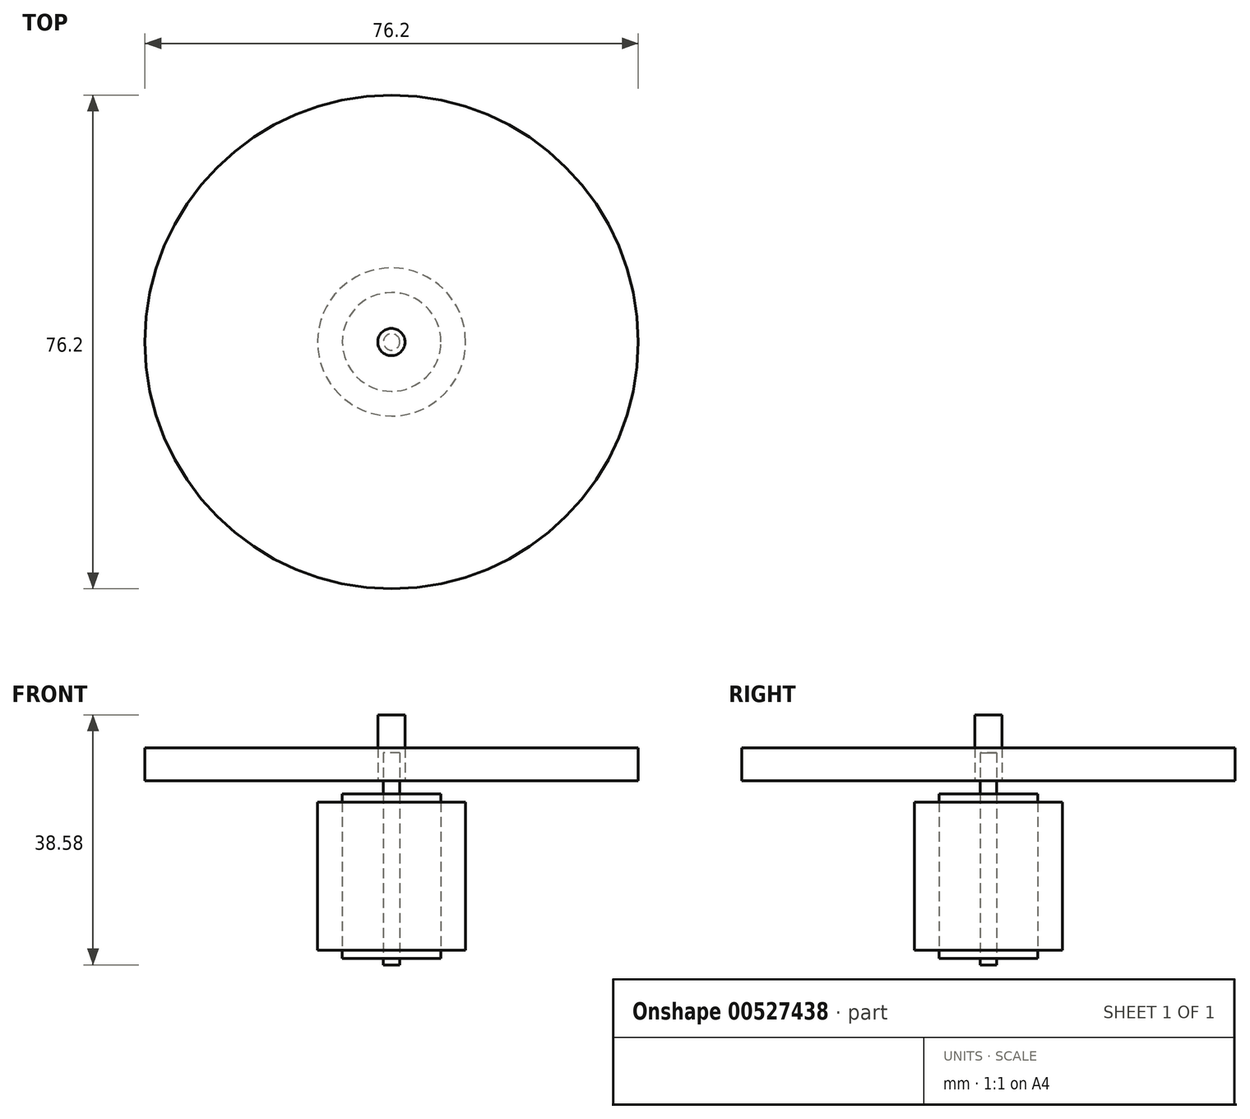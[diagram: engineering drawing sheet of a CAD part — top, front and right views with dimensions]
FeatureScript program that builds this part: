
annotation { "Feature Type Name" : "Feature", "Feature Type Description" : "" }
export const myFeature = defineFeature(function(context is Context, id is Id, definition is map)
    precondition{}
    {
        {
            var Q0;
            Q0=qCreatedBy(makeId("Top.planeOp"),FACE);
            var sketch = newSketch(context, id + "F0", { "sketchPlane" : qUnion([Q0])});
            skCircle(sketch, "E0", {"center": v(0, 0) * mm, "radius": 11.43 * mm});
            skSolve(sketch);
        }
        {
            var Q0;
            Q0=qCreatedBy(makeId("Top.planeOp"),FACE);
            var sketch = newSketch(context, id + "F1", { "sketchPlane" : qUnion([Q0])});
            skCircle(sketch, "E1", {"center": v(0, 0) * mm, "radius": 7.62 * mm});
            skSolve(sketch);
        }
        {
            var Q0;
            Q0=makeQuery(id+"F0.imprint","IMPRINT",FACE,{"disambiguationData":[TD([[makeQuery(id+"F0.imprint","IMPRINT",EDGE,{"derivedFrom":sQuery(id+"F0.wireOp",EDGE,"E0")}),1.0]])]});
            var Q1;
            Q1=sQuery(id+"F0.wireOp",EDGE,"E0");
            extrude(context, id + "F2", {"entities" : qUnion([Q0]), "surfaceEntities" : qUnion([Q1]), "endBound" : BoundingType.SYMMETRIC, "depth" : 22.86 * mm, "offsetDistance" : 25.4 * mm});
        }
        {
            var Q0;
            Q0=makeQuery(id+"F1.imprint","IMPRINT",FACE,{"disambiguationData":[TD([[makeQuery(id+"F1.imprint","IMPRINT",EDGE,{"derivedFrom":sQuery(id+"F1.wireOp",EDGE,"E1")}),1.0]])]});
            var Q1;
            Q1=sQuery(id+"F1.wireOp",EDGE,"E1");
            extrude(context, id + "F3", {"entities" : qUnion([Q0]), "surfaceEntities" : qUnion([Q1]), "endBound" : BoundingType.SYMMETRIC, "depth" : 25.4 * mm, "offsetDistance" : 25.4 * mm});
        }
        {
            var Q0;
            Q0=qCreatedBy(makeId("Top.planeOp"),FACE);
            var sketch = newSketch(context, id + "F4", { "sketchPlane" : qUnion([Q0])});
            skCircle(sketch, "E2", {"center": v(0, 0) * mm, "radius": 1.27 * mm});
            skSolve(sketch);
        }
        {
            var Q0;
            Q0 = qSketchRegion(id + "F4", true);
            extrude(context, id + "F5", {"entities" : qUnion([Q0]), "endBound" : BoundingType.SYMMETRIC, "depth" : 38.1 * mm, "offsetDistance" : 25.4 * mm});
        }
        {
            var Q0;
            Q0=qCreatedBy(makeId("Right.planeOp"),FACE);
            var sketch = newSketch(context, id + "F6", { "sketchPlane" : qUnion([Q0])});
            skLineSegment(sketch, "E3.bottom", {"start": v(-55.72, -6.19) * mm, "end": v(-41.53, -6.19) * mm});
            skLineSegment(sketch, "E3.top", {"start": v(-55.72, 0.79) * mm, "end": v(-41.53, 0.79) * mm});
            skLineSegment(sketch, "E3.left", {"start": v(-55.72, -6.19) * mm, "end": v(-55.72, 0.79) * mm});
            skLineSegment(sketch, "E3.right", {"start": v(-41.53, -6.19) * mm, "end": v(-41.53, 0.79) * mm});
            skSolve(sketch);
        }
        {
            var Q0;
            Q0=makeQuery(id+"F6.imprint","IMPRINT",FACE,{"disambiguationData":[TD([[makeQuery(id+"F6.imprint","IMPRINT",EDGE,{"derivedFrom":sQuery(id+"F6.wireOp",EDGE,"E3.bottom")}),1.0]])]});
            extrude(context, id + "F7", {"entities" : qUnion([Q0]), "endBound" : BoundingType.SYMMETRIC, "depth" : 25.4 * mm, "offsetDistance" : 25.4 * mm});
        }
        {
            var Q0;
            Q0=makeQuery(id+"F7.opExtrude","SWEPT_BODY",BODY,{"disambiguationData":[OSD([sQuery(id+"F6.wireOp",EDGE,"E3.bottom"),sQuery(id+"F6.wireOp",EDGE,"E3.top"),sQuery(id+"F6.wireOp",EDGE,"E3.left"),sQuery(id+"F6.wireOp",EDGE,"E3.right")])]});
            transform(context, id + "F8", {"entities" : qUnion([Q0]), "transformType" : TransformType.TRANSLATION_3D, "dx" : 0 * mm, "dy" : 50.8 * mm, "dz" : -14.48 * mm, "makeCopy" : false});
        }
        {
            var Q0;
            Q0=makeQuery(id+"F7.opExtrude","SWEPT_BODY",BODY,{"disambiguationData":[OSD([sQuery(id+"F6.wireOp",EDGE,"E3.bottom"),sQuery(id+"F6.wireOp",EDGE,"E3.top"),sQuery(id+"F6.wireOp",EDGE,"E3.left"),sQuery(id+"F6.wireOp",EDGE,"E3.right")])]});
            var Q1;
            Q1=makeQuery(id+"F5.opExtrude","SWEPT_BODY",BODY,{"disambiguationData":[OSD([sQuery(id+"F4.wireOp",EDGE,"E2")])]});
            booleanBodies(context, id + "F9", {"operationType" : BooleanOperationType.SUBTRACTION, "tools" : qUnion([Q0]), "targets" : qUnion([Q1])});
        }
        {
            var Q0;
            Q0=qCreatedBy(makeId("Top.planeOp"),FACE);
            var sketch = newSketch(context, id + "F10", { "sketchPlane" : qUnion([Q0])});
            skCircle(sketch, "E4", {"center": v(10.9, 5.29) * mm, "radius": 2.1 * mm});
            skSolve(sketch);
        }
        {
            var Q0;
            Q0=makeQuery(id+"F10.imprint","IMPRINT",FACE,{"disambiguationData":[TD([[makeQuery(id+"F10.imprint","IMPRINT",EDGE,{"derivedFrom":sQuery(id+"F10.wireOp",EDGE,"E4")}),1.0]])]});
            extrude(context, id + "F11", {"entities" : qUnion([Q0]), "depth" : 10.16 * mm, "offsetDistance" : 25.4 * mm});
        }
        {
            var Q0;
            Q0=makeQuery(id+"F11.opExtrude","SWEPT_BODY",BODY,{"disambiguationData":[OSD([sQuery(id+"F10.wireOp",EDGE,"E4")])]});
            transform(context, id + "F12", {"entities" : qUnion([Q0]), "transformType" : TransformType.TRANSLATION_3D, "dx" : -10.92 * mm, "dy" : -5.3 * mm, "dz" : 10.67 * mm, "makeCopy" : false});
        }
        {
            var Q0;
            Q0=qCreatedBy(makeId("Top.planeOp"),FACE);
            var sketch = newSketch(context, id + "F13", { "sketchPlane" : qUnion([Q0])});
            skCircle(sketch, "E5", {"center": v(0, 0) * mm, "radius": 38.1 * mm});
            skSolve(sketch);
        }
        {
            var Q0;
            Q0=makeQuery(id+"F13.imprint","IMPRINT",FACE,{"disambiguationData":[TD([[makeQuery(id+"F13.imprint","IMPRINT",EDGE,{"derivedFrom":sQuery(id+"F13.wireOp",EDGE,"E5")}),1.0]])]});
            extrude(context, id + "F14", {"entities" : qUnion([Q0]), "endBound" : BoundingType.SYMMETRIC, "depth" : 5.08 * mm, "offsetDistance" : 25.4 * mm});
        }
        {
            var Q0;
            Q0=makeQuery(id+"F14.opExtrude","SWEPT_BODY",BODY,{"disambiguationData":[OSD([sQuery(id+"F13.wireOp",EDGE,"E5")])]});
            transform(context, id + "F15", {"entities" : qUnion([Q0]), "transformType" : TransformType.TRANSLATION_3D, "dx" : 0 * mm, "dy" : 0 * mm, "dz" : 13.2 * mm, "makeCopy" : false});
        }
        {
            var Q0;
            Q0=makeQuery(id+"F14.opExtrude","SWEPT_BODY",BODY,{"disambiguationData":[OSD([sQuery(id+"F13.wireOp",EDGE,"E5")])]});
            var Q1;
            Q1=makeQuery(id+"F11.opExtrude","SWEPT_BODY",BODY,{"disambiguationData":[OSD([sQuery(id+"F10.wireOp",EDGE,"E4")])]});
            transform(context, id + "F16", {"entities" : qUnion([Q0, Q1]), "transformType" : TransformType.TRANSLATION_3D, "dx" : 0 * mm, "dy" : 0 * mm, "dz" : 4.06 * mm, "makeCopy" : false});
        }
    });
